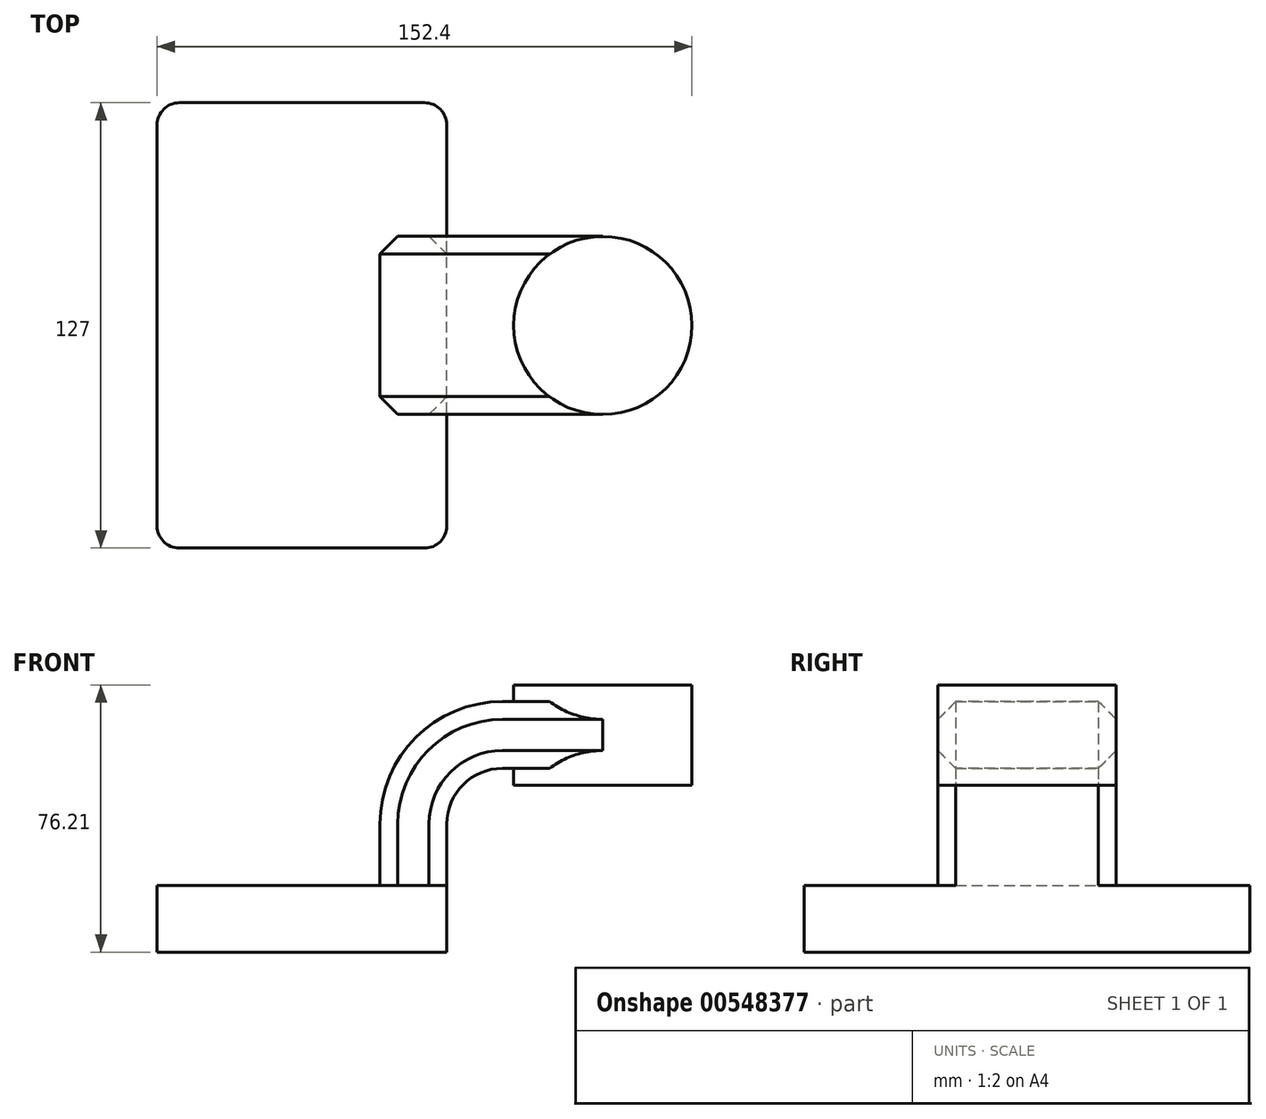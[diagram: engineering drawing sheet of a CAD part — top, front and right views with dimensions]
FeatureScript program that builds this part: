
annotation { "Feature Type Name" : "Feature", "Feature Type Description" : "" }
export const myFeature = defineFeature(function(context is Context, id is Id, definition is map)
    precondition{}
    {
        {
            var Q0;
            Q0=qCreatedBy(makeId("Front.planeOp"),FACE);
            var sketch = newSketch(context, id + "F0", { "sketchPlane" : qUnion([Q0])});
            skLineSegment(sketch, "E0.bottom", {"start": v(41.27, 9.53) * mm, "end": v(-41.28, 9.53) * mm});
            skLineSegment(sketch, "E0.top", {"start": v(41.28, -9.52) * mm, "end": v(-41.27, -9.52) * mm});
            skLineSegment(sketch, "E0.left", {"start": v(41.28, 9.53) * mm, "end": v(41.28, -9.52) * mm});
            skLineSegment(sketch, "E0.right", {"start": v(-41.28, 9.53) * mm, "end": v(-41.27, -9.52) * mm});
            skPoint(sketch, "E0.middle", {"position": v(0, 0) * mm});
            skLineSegment(sketch, "E1.bottom", {"start": v(111.12, 38.1) * mm, "end": v(60.32, 38.1) * mm});
            skLineSegment(sketch, "E1.top", {"start": v(111.12, 66.68) * mm, "end": v(60.32, 66.68) * mm});
            skLineSegment(sketch, "E1.left", {"start": v(111.12, 38.1) * mm, "end": v(111.12, 66.68) * mm});
            skLineSegment(sketch, "E1.right", {"start": v(60.32, 38.1) * mm, "end": v(60.32, 66.68) * mm});
            skPoint(sketch, "E1.middle", {"position": v(85.72, 52.39) * mm});
            skLineSegment(sketch, "E2", {"start": v(41.27, 9.53) * mm, "end": v(41.27, 27) * mm});
            skArc(sketch, "E3", {"start": v(41.27, 27) * mm, "mid": v(45.92, 38.23) * mm, "end": v(57.15, 42.88) * mm});
            skLineSegment(sketch, "E4", {"start": v(57.15, 42.88) * mm, "end": v(85.74, 42.88) * mm});
            skLineSegment(sketch, "E5.0", {"start": v(57.15, 61.93) * mm, "end": v(85.74, 61.93) * mm});
            skArc(sketch, "E5.1", {"start": v(22.23, 27) * mm, "mid": v(32.45, 51.7) * mm, "end": v(57.15, 61.93) * mm});
            skLineSegment(sketch, "E5.2", {"start": v(22.22, 9.53) * mm, "end": v(22.22, 27) * mm});
            skLineSegment(sketch, "E6", {"start": v(85.74, 38.1) * mm, "end": v(85.74, 66.68) * mm});
            skFitSpline(sketch, "E7", {"points": [v(-41.28, 9.53) * mm, v(57.15, 61.93) * mm], "startDerivative": vector(0, 118.5) * mm, "endDerivative": vector(171.45, 0) * mm});
            skSolve(sketch);
        }
        {
            var Q0;
            Q0=makeQuery(id+"F0.imprint","IMPRINT",FACE,{"disambiguationData":[TD([[makeQuery(id+"F0.imprint","IMPRINT",EDGE,{"derivedFrom":sQuery(id+"F0.wireOp",EDGE,"E0.top")}),-1.0]])]});
            extrude(context, id + "F1", {"entities" : qUnion([Q0]), "endBound" : BoundingType.SYMMETRIC, "depth" : 127 * mm, "offsetDistance" : 25.4 * mm});
        }
        {
            var Q0;
            {var subQ1=sQuery(id+"F0.wireOp",EDGE,"E2");Q0=makeQuery(id+"F0.imprint","IMPRINT",FACE,{"disambiguationData":[TD([[makeQuery(id+"F0.imprint","IMPRINT",EDGE,{"derivedFrom":subQ1}),1.0]])]});}
            var Q1;
            {var subQ0=sQuery(id+"F0.wireOp",EDGE,"E4");var subQ1=sQuery(id+"F0.wireOp",EDGE,"E1.right");var subQ2=makeQuery(id+"F0.imprint","INTERSECT",VERTEX,{"derivedFrom":[subQ1,subQ0]});Q1=makeQuery(id+"F0.imprint","IMPRINT",FACE,{"disambiguationData":[TD([[makeQuery(id+"F0.imprint","IMPRINT",EDGE,{"disambiguationData":[TD([[subQ2,-1.0]])],"derivedFrom":subQ1}),-1.0]])]});}
            extrude(context, id + "F2", {"entities" : qUnion([Q0, Q1]), "operationType" : NewBodyOperationType.ADD, "endBound" : BoundingType.SYMMETRIC, "depth" : 50.8 * mm, "offsetDistance" : 25.4 * mm});
        }
        {
            var Q0;
            Q0=makeQuery(id+"F0.imprint","IMPRINT",FACE,{"disambiguationData":[TD([[makeQuery(id+"F0.imprint","IMPRINT",EDGE,{"derivedFrom":sQuery(id+"F0.wireOp",EDGE,"E5.1")}),1.0]])]});
            extrude(context, id + "F3", {"entities" : qUnion([Q0]), "operationType" : NewBodyOperationType.ADD, "endBound" : BoundingType.SYMMETRIC, "depth" : 15.88 * mm, "offsetDistance" : 25.4 * mm});
        }
        {
            var Q0;
            {var subQ4=sQuery(id+"F0.wireOp",EDGE,"E1.left");Q0=makeQuery(id+"F0.imprint","IMPRINT",FACE,{"disambiguationData":[TD([[makeQuery(id+"F0.imprint","IMPRINT",EDGE,{"derivedFrom":subQ4}),1.0]])]});}
            var Q1;
            Q1=sQuery(id+"F0.wireOp",EDGE,"E6");
            revolve(context, id + "F4", {"operationType" : NewBodyOperationType.ADD, "entities" : qUnion([Q0]), "axis" : qUnion([Q1]), "revolveType" : RevolveType.FULL});
        }
        {
            var Q0;
            Q0=makeQuery(id+"F1.opExtrude","CAP_EDGE",EDGE,{"disambiguationData":[OSD([sQuery(id+"F0.wireOp",EDGE,"E0.right")])],"isStart":false});
            var Q1;
            Q1=makeQuery(id+"F1.opExtrude","CAP_EDGE",EDGE,{"disambiguationData":[OSD([sQuery(id+"F0.wireOp",EDGE,"E0.left")])],"isStart":false});
            var Q2;
            Q2=makeQuery(id+"F1.opExtrude","CAP_EDGE",EDGE,{"disambiguationData":[OSD([sQuery(id+"F0.wireOp",EDGE,"E0.left")])],"isStart":true});
            var Q3;
            Q3=makeQuery(id+"F1.opExtrude","CAP_EDGE",EDGE,{"disambiguationData":[OSD([sQuery(id+"F0.wireOp",EDGE,"E0.right")])],"isStart":true});
            fillet(context, id + "F5", {"entities" : qUnion([Q0, Q1, Q2, Q3]), "radius" : 6.35 * mm, "tangentPropagation" : true, "allowEdgeOverflow" : false});
        }
        {
            var Q0;
            Q0=makeQuery(id+"F2.opExtrude","CAP_EDGE",EDGE,{"disambiguationData":[OSD([sQuery(id+"F0.wireOp",EDGE,"E5.1")])],"isStart":true});
            var Q1;
            Q1=makeQuery(id+"F2.opExtrude","CAP_EDGE",EDGE,{"disambiguationData":[OSD([sQuery(id+"F0.wireOp",EDGE,"E5.1")])],"isStart":false});
            var Q2;
            Q2=makeQuery(id+"F2.opExtrude","CAP_EDGE",EDGE,{"disambiguationData":[OSD([sQuery(id+"F0.wireOp",EDGE,"E3")])],"isStart":false});
            var Q3;
            Q3=makeQuery(id+"F2.opExtrude","CAP_EDGE",EDGE,{"disambiguationData":[OSD([sQuery(id+"F0.wireOp",EDGE,"E3")])],"isStart":true});
            chamfer(context, id + "F6", {"entities" : qUnion([Q0, Q1, Q2, Q3]), "width" : 5.08 * mm, "tangentPropagation" : true});
        }
    });
